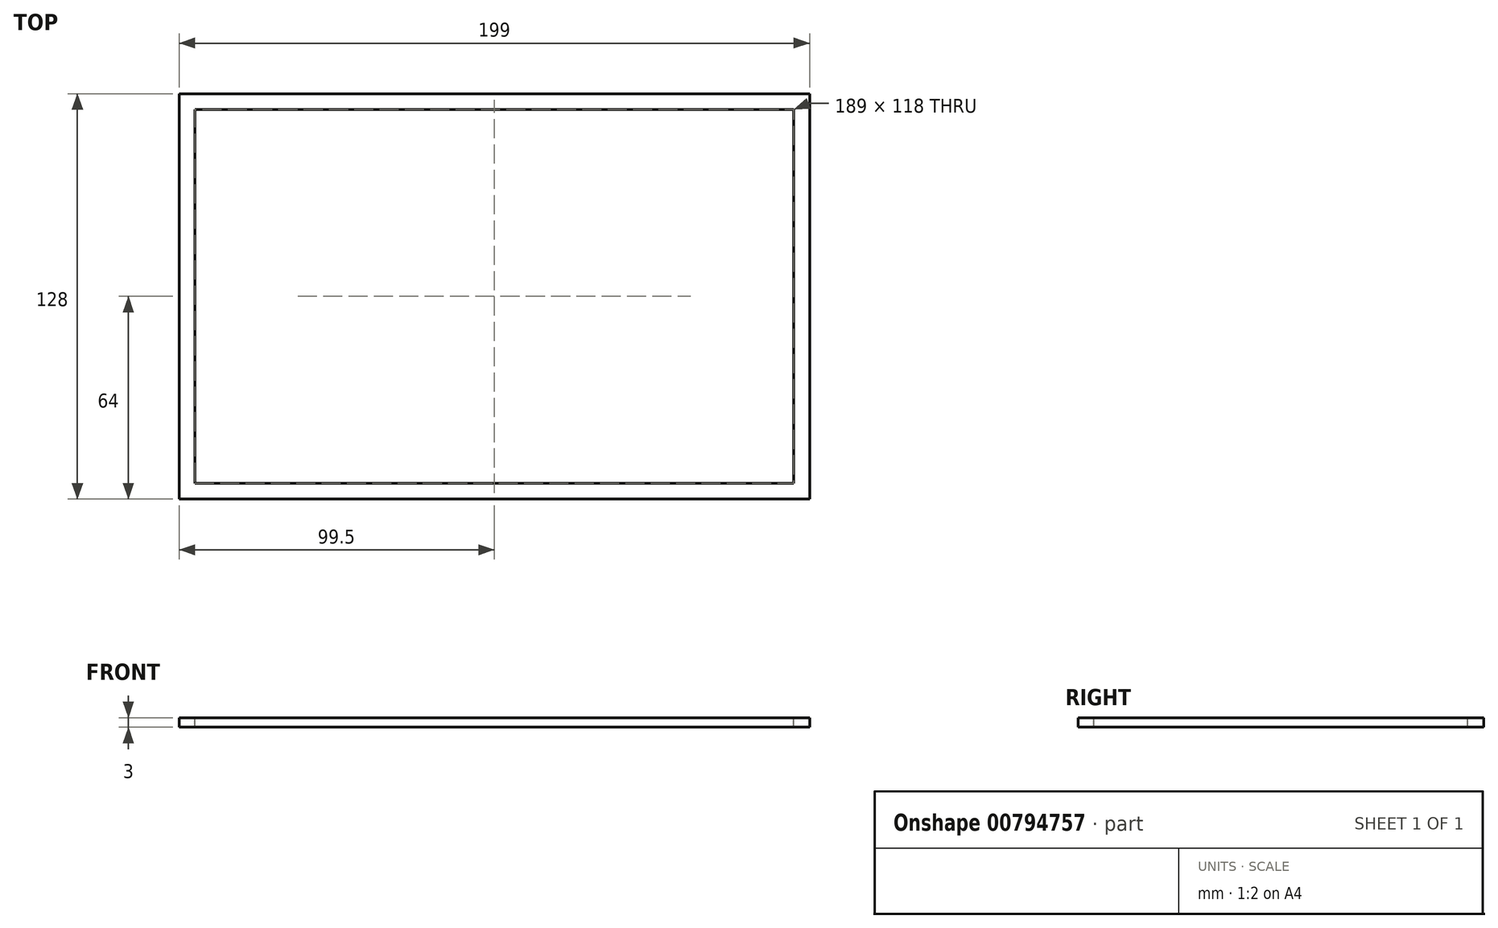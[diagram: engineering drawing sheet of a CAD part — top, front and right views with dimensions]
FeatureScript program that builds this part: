
annotation { "Feature Type Name" : "Feature", "Feature Type Description" : "" }
export const myFeature = defineFeature(function(context is Context, id is Id, definition is map)
    precondition{}
    {
        {
            var Q0;
            Q0=qCreatedBy(makeId("Top.planeOp"),FACE);
            var sketch = newSketch(context, id + "F0", { "sketchPlane" : qUnion([Q0])});
            skLineSegment(sketch, "E0.bottom", {"start": v(99.5, -64) * mm, "end": v(-99.5, -64) * mm});
            skLineSegment(sketch, "E0.top", {"start": v(99.5, 64) * mm, "end": v(-99.5, 64) * mm});
            skLineSegment(sketch, "E0.left", {"start": v(99.5, -64) * mm, "end": v(99.5, 64) * mm});
            skLineSegment(sketch, "E0.right", {"start": v(-99.5, -64) * mm, "end": v(-99.5, 64) * mm});
            skPoint(sketch, "E0.middle", {"position": v(0, 0) * mm});
            skSolve(sketch);
        }
        {
            var Q0;
            Q0 = qSketchRegion(id + "F0", true);
            extrude(context, id + "F1", {"entities" : qUnion([Q0]), "depth" : 3 * mm, "offsetDistance" : 25 * mm});
        }
        {
            var Q0;
            Q0=makeQuery(id+"F1.opExtrude","CAP_FACE",FACE,{"disambiguationData":[OSD([sQuery(id+"F0.wireOp",EDGE,"E0.bottom"),sQuery(id+"F0.wireOp",EDGE,"E0.top"),sQuery(id+"F0.wireOp",EDGE,"E0.left"),sQuery(id+"F0.wireOp",EDGE,"E0.right")])],"isStart":false});
            var sketch = newSketch(context, id + "F2", { "sketchPlane" : qUnion([Q0])});
            skLineSegment(sketch, "E1.bottom", {"start": v(94.5, -59) * mm, "end": v(-94.5, -59) * mm});
            skLineSegment(sketch, "E1.top", {"start": v(94.5, 59) * mm, "end": v(-94.5, 59) * mm});
            skLineSegment(sketch, "E1.left", {"start": v(94.5, -59) * mm, "end": v(94.5, 59) * mm});
            skLineSegment(sketch, "E1.right", {"start": v(-94.5, -59) * mm, "end": v(-94.5, 59) * mm});
            skPoint(sketch, "E1.middle", {"position": v(0, 0) * mm});
            skSolve(sketch);
        }
        {
            var Q0;
            Q0 = qSketchRegion(id + "F2", true);
            extrude(context, id + "F3", {"entities" : qUnion([Q0]), "operationType" : NewBodyOperationType.REMOVE, "endBound" : BoundingType.THROUGH_ALL, "oppositeDirection" : true, "depth" : 25 * mm, "offsetDistance" : 25 * mm});
        }
    });
